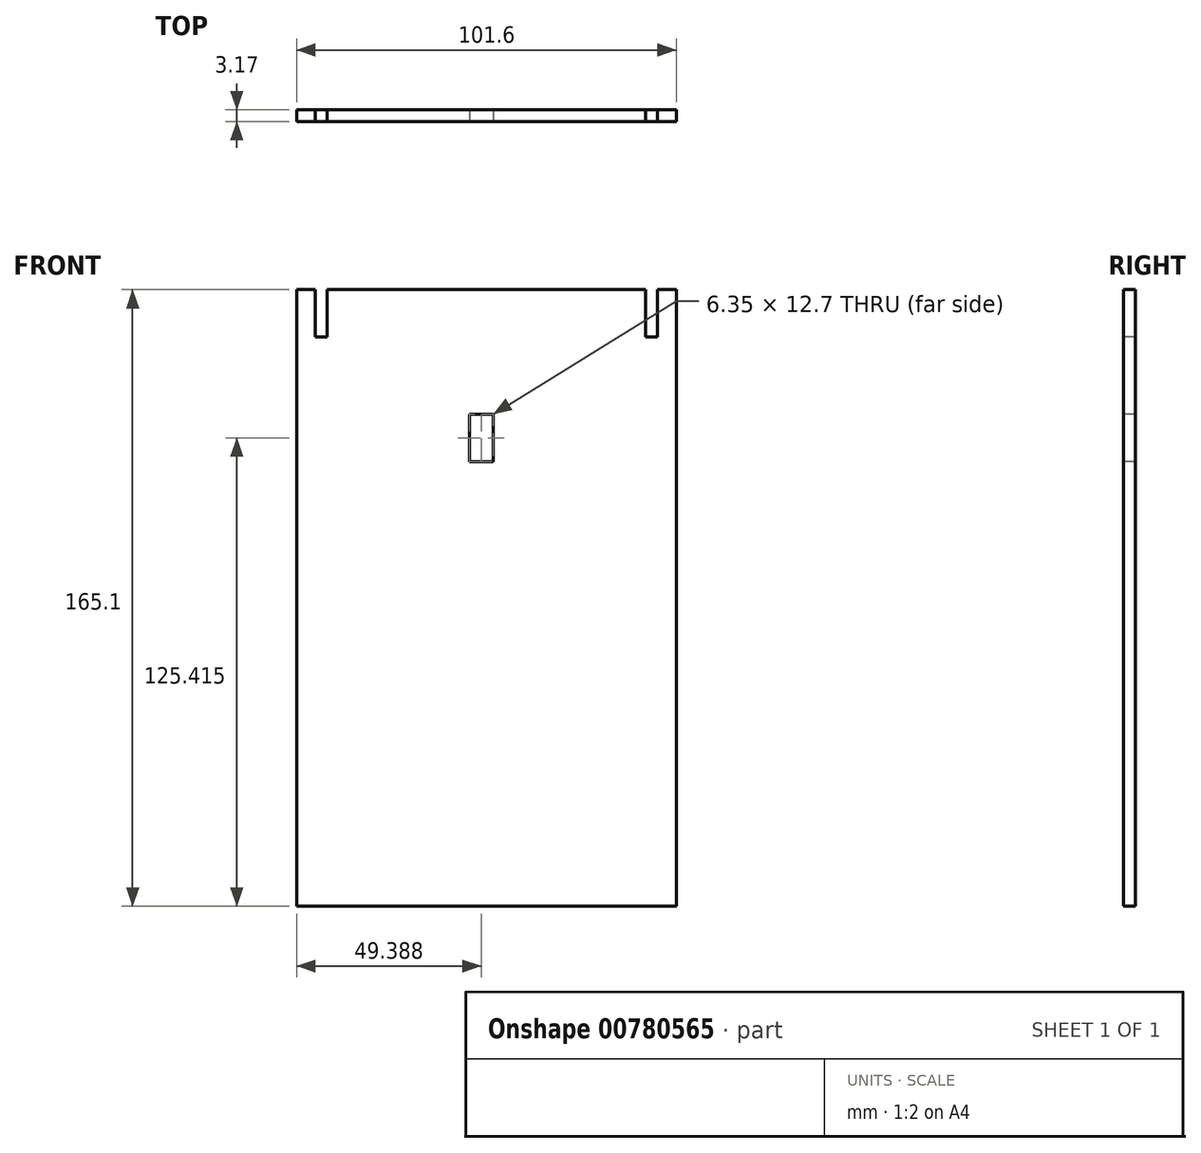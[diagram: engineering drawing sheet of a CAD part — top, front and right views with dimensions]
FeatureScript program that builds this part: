
annotation { "Feature Type Name" : "Feature", "Feature Type Description" : "" }
export const myFeature = defineFeature(function(context is Context, id is Id, definition is map)
    precondition{}
    {
        {
            var Q0;
            Q0=qCreatedBy(makeId("Front.planeOp"),FACE);
            var sketch = newSketch(context, id + "F0", { "sketchPlane" : qUnion([Q0])});
            skLineSegment(sketch, "E0.bottom", {"start": v(-91.76, 126.41) * mm, "end": v(-86.76, 126.41) * mm});
            skLineSegment(sketch, "E0.top", {"start": v(-91.76, -38.69) * mm, "end": v(9.84, -38.69) * mm});
            skLineSegment(sketch, "E0.left", {"start": v(-91.76, 126.41) * mm, "end": v(-91.76, -38.69) * mm});
            skLineSegment(sketch, "E0.right", {"start": v(9.84, 126.41) * mm, "end": v(9.84, -38.69) * mm});
            skLineSegment(sketch, "E1.top", {"start": v(-86.76, 113.71) * mm, "end": v(-83.56, 113.71) * mm});
            skLineSegment(sketch, "E1.left", {"start": v(-86.76, 126.41) * mm, "end": v(-86.76, 113.71) * mm});
            skLineSegment(sketch, "E1.right", {"start": v(-83.56, 126.41) * mm, "end": v(-83.56, 113.71) * mm});
            skLineSegment(sketch, "E2.top", {"start": v(4.84, 113.71) * mm, "end": v(1.64, 113.71) * mm});
            skLineSegment(sketch, "E2.left", {"start": v(4.84, 126.41) * mm, "end": v(4.84, 113.71) * mm});
            skLineSegment(sketch, "E2.right", {"start": v(1.64, 126.41) * mm, "end": v(1.64, 113.71) * mm});
            skLineSegment(sketch, "E3.trimOffspring", {"start": v(-83.56, 126.41) * mm, "end": v(1.64, 126.41) * mm});
            skLineSegment(sketch, "E4.trimOffspring", {"start": v(4.84, 126.41) * mm, "end": v(9.84, 126.41) * mm});
            skLineSegment(sketch, "E5.bottom", {"start": v(-68.65, 66.05) * mm, "end": v(-15.31, 66.05) * mm});
            skLineSegment(sketch, "E5.top", {"start": v(-68.65, -7.6) * mm, "end": v(-15.31, -7.6) * mm});
            skLineSegment(sketch, "E5.left", {"start": v(-68.65, 66.05) * mm, "end": v(-68.65, -7.6) * mm});
            skLineSegment(sketch, "E5.right", {"start": v(-15.31, 66.05) * mm, "end": v(-15.31, -7.6) * mm});
            skLineSegment(sketch, "E6.bottom", {"start": v(-45.55, 93.08) * mm, "end": v(-39.2, 93.08) * mm});
            skLineSegment(sketch, "E6.top", {"start": v(-45.55, 80.38) * mm, "end": v(-39.2, 80.38) * mm});
            skLineSegment(sketch, "E6.left", {"start": v(-45.55, 93.08) * mm, "end": v(-45.55, 80.38) * mm});
            skLineSegment(sketch, "E6.right", {"start": v(-39.2, 93.08) * mm, "end": v(-39.2, 80.38) * mm});
            skSolve(sketch);
        }
        {
            var Q0;
            Q0=makeQuery(id+"F0.imprint","IMPRINT",FACE,{"disambiguationData":[TD([[makeQuery(id+"F0.imprint","IMPRINT",EDGE,{"derivedFrom":sQuery(id+"F0.wireOp",EDGE,"E0.bottom")}),-1.0]])]});
            var Q1;
            Q1=makeQuery(id+"F0.imprint","IMPRINT",FACE,{"disambiguationData":[TD([[makeQuery(id+"F0.imprint","IMPRINT",EDGE,{"derivedFrom":sQuery(id+"F0.wireOp",EDGE,"E5.bottom")}),-1.0]])]});
            extrude(context, id + "F1", {"entities" : qUnion([Q0, Q1]), "oppositeDirection" : true, "depth" : 3.17 * mm, "offsetDistance" : 25.4 * mm});
        }
    });
